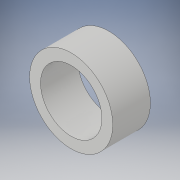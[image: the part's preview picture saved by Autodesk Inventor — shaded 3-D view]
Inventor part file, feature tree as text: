
AUTODESK INVENTOR PART (.ipt)
format: ipt  version: 2019 (Build 230136000, 136)  size: 102,400 bytes
history: native  units: mm
features: extrude x2, sketch x2
ambient origin geometry x8: Origin, YZ Plane, XZ Plane, XY Plane, X Axis, Y Axis, Z Axis, Center Point
bodies: Solid1 (feature_tree)
feature tree (4):
  extrude  "Extrusion1"  Depth=95.0mm TaperAngle=0.0deg
  extrude  "Extrusion2"  Depth=9.5mm TaperAngle=0.0deg
  sketch  "Sketch1"  dims[d0=210.0mm d1=95.0mm d2=0.0mm]
  sketch  "Sketch2"  dims[d3=155.0mm d4=9.5mm d5=0.0mm]
